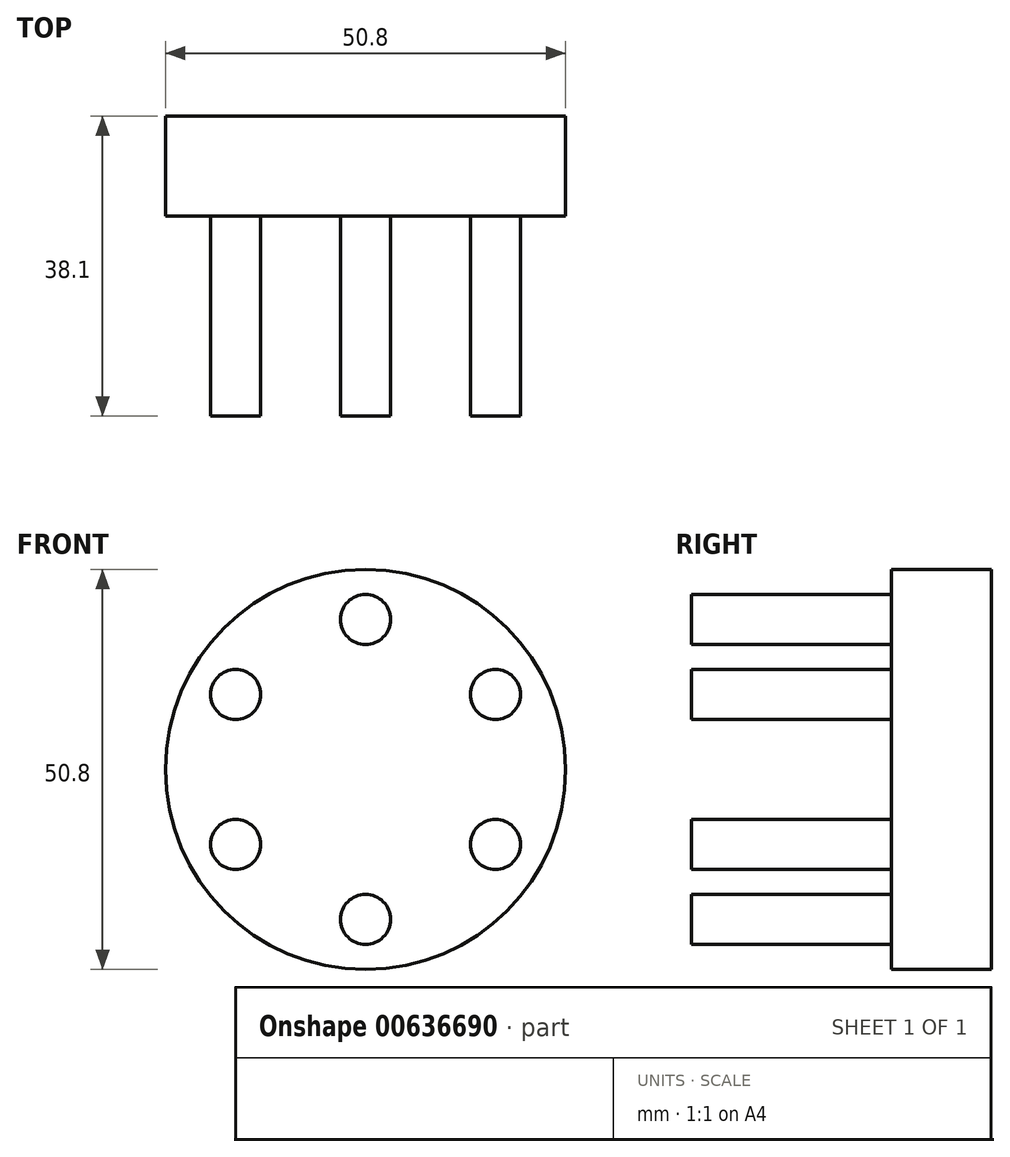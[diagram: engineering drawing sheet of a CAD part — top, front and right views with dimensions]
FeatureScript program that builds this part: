
annotation { "Feature Type Name" : "Feature", "Feature Type Description" : "" }
export const myFeature = defineFeature(function(context is Context, id is Id, definition is map)
    precondition{}
    {
        {
            var Q0;
            Q0=qCreatedBy(makeId("Front.planeOp"),FACE);
            var sketch = newSketch(context, id + "F0", { "sketchPlane" : qUnion([Q0])});
            skCircle(sketch, "E0", {"center": v(0, 0) * mm, "radius": 25.4 * mm});
            skSolve(sketch);
        }
        {
            var Q0;
            Q0=makeQuery(id+"F0.imprint","IMPRINT",FACE,{"disambiguationData":[TD([[makeQuery(id+"F0.imprint","IMPRINT",EDGE,{"derivedFrom":sQuery(id+"F0.wireOp",EDGE,"E0")}),1.0]])]});
            extrude(context, id + "F1", {"entities" : qUnion([Q0]), "depth" : 12.7 * mm, "offsetDistance" : 25.4 * mm});
        }
        {
            var Q0;
            Q0=makeQuery(id+"F1.opExtrude","CAP_FACE",FACE,{"disambiguationData":[OSD([sQuery(id+"F0.wireOp",EDGE,"E0")])],"isStart":false});
            var sketch = newSketch(context, id + "F2", { "sketchPlane" : qUnion([Q0])});
            skLineSegment(sketch, "E1", {"start": v(0, 25.4) * mm, "end": v(0, 19.05) * mm});
            skCircle(sketch, "E2", {"center": v(0, 19.05) * mm, "radius": 3.18 * mm});
            skCircle(sketch, "E3.1.0", {"center": v(-16.5, 9.53) * mm, "radius": 3.18 * mm});
            skCircle(sketch, "E3.2.0", {"center": v(-16.5, -9.52) * mm, "radius": 3.18 * mm});
            skCircle(sketch, "E3.3.0", {"center": v(0, -19.05) * mm, "radius": 3.18 * mm});
            skCircle(sketch, "E3.4.0", {"center": v(16.5, -9.53) * mm, "radius": 3.18 * mm});
            skCircle(sketch, "E3.5.0", {"center": v(16.5, 9.53) * mm, "radius": 3.18 * mm});
            skPoint(sketch, "E3.center", {"position": v(0, 0) * mm});
            skSolve(sketch);
        }
        {
            var Q0;
            Q0=makeQuery(id+"F2.imprint","IMPRINT",FACE,{"disambiguationData":[TD([[makeQuery(id+"F2.imprint","IMPRINT",EDGE,{"derivedFrom":sQuery(id+"F2.wireOp",EDGE,"E3.1.0")}),1.0]])]});
            var Q1;
            Q1=makeQuery(id+"F2.imprint","IMPRINT",FACE,{"disambiguationData":[TD([[makeQuery(id+"F2.imprint","IMPRINT",EDGE,{"derivedFrom":sQuery(id+"F2.wireOp",EDGE,"E2")}),1.0]])]});
            var Q2;
            Q2=makeQuery(id+"F2.imprint","IMPRINT",FACE,{"disambiguationData":[TD([[makeQuery(id+"F2.imprint","IMPRINT",EDGE,{"derivedFrom":sQuery(id+"F2.wireOp",EDGE,"E3.5.0")}),1.0]])]});
            var Q3;
            Q3=makeQuery(id+"F2.imprint","IMPRINT",FACE,{"disambiguationData":[TD([[makeQuery(id+"F2.imprint","IMPRINT",EDGE,{"derivedFrom":sQuery(id+"F2.wireOp",EDGE,"E3.4.0")}),1.0]])]});
            var Q4;
            Q4=makeQuery(id+"F2.imprint","IMPRINT",FACE,{"disambiguationData":[TD([[makeQuery(id+"F2.imprint","IMPRINT",EDGE,{"derivedFrom":sQuery(id+"F2.wireOp",EDGE,"E3.3.0")}),1.0]])]});
            var Q5;
            Q5=makeQuery(id+"F2.imprint","IMPRINT",FACE,{"disambiguationData":[TD([[makeQuery(id+"F2.imprint","IMPRINT",EDGE,{"derivedFrom":sQuery(id+"F2.wireOp",EDGE,"E3.2.0")}),1.0]])]});
            extrude(context, id + "F3", {"entities" : qUnion([Q0, Q1, Q2, Q3, Q4, Q5]), "operationType" : NewBodyOperationType.ADD, "depth" : 25.4 * mm, "offsetDistance" : 25.4 * mm});
        }
    });
